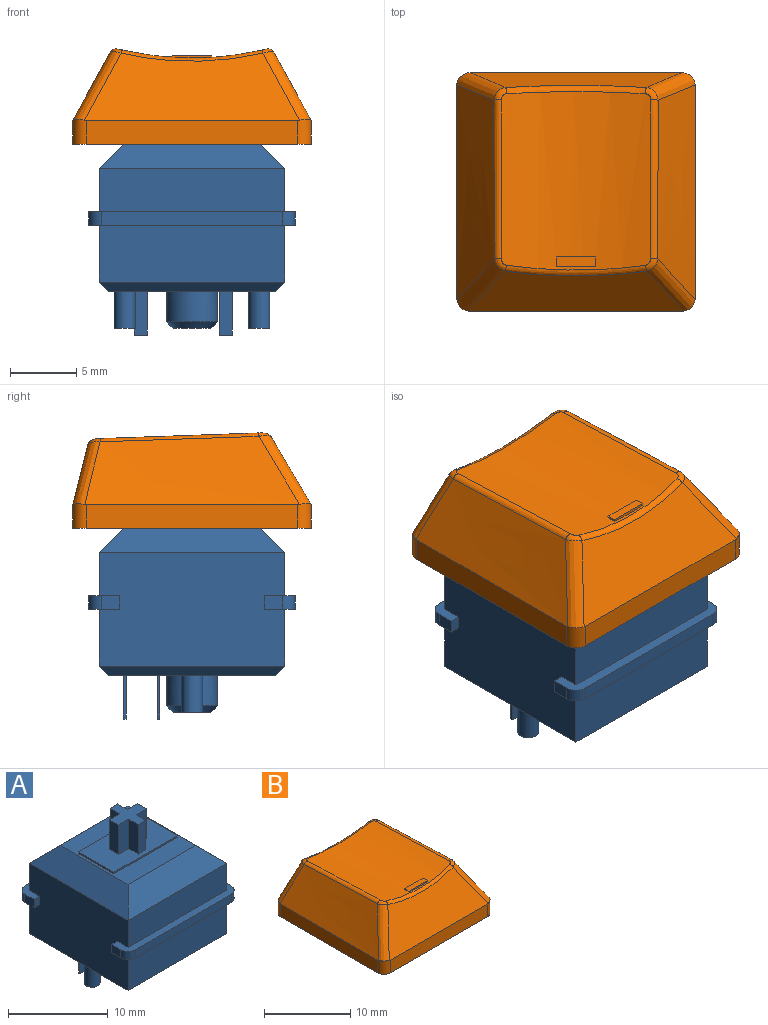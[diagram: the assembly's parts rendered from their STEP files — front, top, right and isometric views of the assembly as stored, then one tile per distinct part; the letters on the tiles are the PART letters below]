
ASSEMBLY  parts=2 mates=1
PART A: 69 faces, bbox 15.6x15.6x18.6 mm
  f0: plane 15.6x2.3mm, normal (0,0,-1), area 14.4mm2, adj f2,f3,f28,f30,f35,f60,f62,f63
  f1: plane 15.6x2.3mm, normal (0,0,-1), area 14.4mm2, adj f28,f30,f33,f34,f36,f59,f61,f64
  f2: plane 1.3x1mm, normal (1,0,0), area 1.3mm2, adj f0,f32,f62,f66
  f3: plane 1.3x1mm, normal (-1,0,0), area 1.3mm2, adj f0,f32,f63,f68
  f4: plane 15.6x2.3mm, normal (0,0,1), area 14.4mm2, adj f28,f30,f31,f33,f34,f36,f61,f64
  f5: plane 14x2.2mm, normal (-0.71,0,0.71), area 36.7mm2, adj f6,f7,f26,f30
  f6: plane 14x2.2mm, normal (0,-0.71,0.71), area 36.7mm2, adj f5,f7,f27,f31
  f7: plane 9.6x9.6mm, normal (0,0,1), area 47.2mm2, adj f5,f6,f8,f9,f10,f11,f26,f27
  f8: plane 5x0.2mm, normal (1,0,0), area 1mm2, adj f7,f9,f11,f12
  f9: plane 9x0.2mm, normal (0,1,0), area 1.8mm2, adj f7,f8,f10,f12
  f10: plane 5x0.2mm, normal (-1,0,0), area 1mm2, adj f7,f9,f11,f12
  f11: plane 9x0.2mm, normal (0,-1,0), area 1.8mm2, adj f7,f8,f10,f12
  f12: plane 9x5mm, normal (0,0,1), area 36.9mm2, adj f8,f9,f10,f11,f13,f14,f15,f16
  f13: plane 3.6x1.35mm, normal (1,0,0), area 4.9mm2, adj f12,f14,f24,f25
  f14: plane 3.6x1.08mm, normal (0,1,0), area 3.9mm2, adj f12,f13,f15,f25
  f15: plane 3.6x1.35mm, normal (-1,0,0), area 4.9mm2, adj f12,f14,f16,f25
  f16: plane 3.6x1.46mm, normal (0,1,0), area 5.3mm2, adj f12,f15,f17,f25
  f17: plane 3.6x1.3mm, normal (-1,0,0), area 4.7mm2, adj f12,f16,f18,f25
  f18: plane 3.6x1.46mm, normal (0,-1,0), area 5.3mm2, adj f12,f17,f19,f25
  f19: plane 3.6x1.35mm, normal (-1,0,0), area 4.9mm2, adj f12,f18,f20,f25
  f20: plane 3.6x1.08mm, normal (0,-1,0), area 3.9mm2, adj f12,f19,f21,f25
  f21: plane 3.6x1.35mm, normal (1,0,0), area 4.9mm2, adj f12,f20,f22,f25
  f22: plane 3.6x1.46mm, normal (0,-1,0), area 5.3mm2, adj f12,f21,f23,f25
  f23: plane 3.6x1.3mm, normal (1,0,0), area 4.7mm2, adj f12,f22,f24,f25
  f24: plane 3.6x1.46mm, normal (0,1,0), area 5.3mm2, adj f12,f13,f23,f25
  f25: plane 4x4mm, normal (0,0,1), area 8.1mm2, adj f13,f14,f15,f16,f17,f18,f19,f20
  f26: plane 14x2.2mm, normal (0,0.71,0.71), area 36.7mm2, adj f5,f7,f27,f29
  f27: plane 14x2.2mm, normal (0.71,0,0.71), area 36.7mm2, adj f6,f7,f26,f28
  f28: plane 14x8.6mm, normal (1,0,0), area 117.4mm2, adj f0,f1,f4,f27,f29,f31,f32,f55
  f29: plane 14x3.3mm, normal (0,1,0), area 46.2mm2, adj f26,f28,f30,f32
  f30: plane 14x8.6mm, normal (-1,0,0), area 117.4mm2, adj f0,f1,f4,f5,f29,f31,f32,f57
  f31: plane 14x3.3mm, normal (0,-1,0), area 46.2mm2, adj f4,f6,f28,f30
  f32: plane 15.6x2.3mm, normal (0,0,1), area 14.4mm2, adj f2,f3,f28,f29,f30,f35,f62,f63
  f33: plane 13.6x1mm, normal (0,-1,0), area 13.6mm2, adj f1,f4,f61,f64
  f34: plane 1.3x1mm, normal (1,0,0), area 1.3mm2, adj f1,f4,f61,f65
  f35: plane 13.6x1mm, normal (0,1,0), area 13.6mm2, adj f0,f32,f62,f63
  f36: plane 1.3x1mm, normal (-1,0,0), area 1.3mm2, adj f1,f4,f64,f67
  f37: plane 2.85x2.85mm, normal (0,0,-1), area 6.4mm2, adj f38
  f38: cone r=1.43mm half-angle=45deg, axis (0,0,1), area 7.4mm2, adj f37,f43
  f39: plane 1x0.2mm, normal (0,0,-1), area 0.2mm2, adj f44,f45,f46,f47
  f40: plane 1x0.2mm, normal (0,0,-1), area 0.2mm2, adj f48,f49,f50,f51
  f41: plane 1.6x1.6mm, normal (0,0,-1), area 2mm2, adj f52
  f42: plane 1.6x1.6mm, normal (0,0,-1), area 2mm2, adj f53
  f43: cylinder r=1.93mm len=3.85mm, axis (0,0,1), area 27.8mm2, adj f38,f54
  f44: plane 3.3x0.2mm, normal (-1,0,0), area 0.7mm2, adj f39,f45,f47,f54
  f45: plane 3.3x1mm, normal (0,1,0), area 3.3mm2, adj f39,f44,f46,f54
  f46: plane 3.3x0.2mm, normal (1,0,0), area 0.7mm2, adj f39,f45,f47,f54
  f47: plane 3.3x1mm, normal (0,-1,0), area 3.3mm2, adj f39,f44,f46,f54
  f48: plane 3.3x0.2mm, normal (-1,0,0), area 0.7mm2, adj f40,f49,f51,f54
  f49: plane 3.3x1mm, normal (0,1,0), area 3.3mm2, adj f40,f48,f50,f54
  f50: plane 3.3x0.2mm, normal (1,0,0), area 0.7mm2, adj f40,f49,f51,f54
  f51: plane 3.3x1mm, normal (0,-1,0), area 3.3mm2, adj f40,f48,f50,f54
  f52: cylinder r=0.8mm len=2.8mm, axis (0,0,1), area 14.1mm2, adj f41,f54
  f53: cylinder r=0.8mm len=2.8mm, axis (0,0,1), area 14.1mm2, adj f42,f54
  f54: plane 12.6x12.6mm, normal (0,0,-1), area 142.7mm2, adj f43,f44,f45,f46,f47,f48,f49,f50
  f55: plane 14x0.7mm, normal (0.71,0,-0.71), area 13.2mm2, adj f28,f54,f56,f58
  f56: plane 14x0.7mm, normal (0,0.71,-0.71), area 13.2mm2, adj f54,f55,f57,f60
  f57: plane 14x0.7mm, normal (-0.71,0,-0.71), area 13.2mm2, adj f30,f54,f56,f58
  f58: plane 14x0.7mm, normal (0,-0.71,-0.71), area 13.2mm2, adj f54,f55,f57,f59
  f59: plane 14x4.3mm, normal (0,-1,0), area 60.2mm2, adj f1,f28,f30,f58
  f60: plane 14x4.3mm, normal (0,1,0), area 60.2mm2, adj f0,f28,f30,f56
  f61: cylinder r=1mm len=1mm, axis (0,0,-1), area 1.6mm2, adj f1,f4,f33,f34
  f62: cylinder r=1mm len=1mm, axis (0,0,1), area 1.6mm2, adj f0,f2,f32,f35
  f63: cylinder r=1mm len=1mm, axis (0,0,-1), area 1.6mm2, adj f0,f3,f32,f35
  f64: cylinder r=1mm len=1mm, axis (0,0,1), area 1.6mm2, adj f1,f4,f33,f36
  f65: plane 1x0.8mm, normal (0,1,0), area 0.8mm2, adj f1,f4,f28,f34
  f66: plane 1x0.8mm, normal (0,-1,0), area 0.8mm2, adj f0,f2,f28,f32
  f67: plane 1x0.8mm, normal (0,1,0), area 0.8mm2, adj f1,f4,f30,f36
  f68: plane 1x0.8mm, normal (0,-1,0), area 0.8mm2, adj f0,f3,f30,f32
PART B: 55 faces, bbox 21.6x21x10.3 mm
  f0: cylinder r=22.9mm len=13.32mm, axis (0,1,-0.04), area 147.4mm2, adj f18,f19,f20,f21,f22,f23,f24,f25
  f1: plane 18x18mm, normal (0,0,-1), area 67.1mm2, adj f2,f3,f4,f5,f10,f12,f14,f16
  f2: plane 16x1.8mm, normal (1,0,0), area 28.8mm2, adj f1,f9,f10,f16
  f3: plane 16x1.8mm, normal (0,1,0), area 28.8mm2, adj f1,f6,f14,f15,f16,f17
  f4: plane 16x1.8mm, normal (-1,0,0), area 28.8mm2, adj f1,f7,f12,f14
  f5: plane 16x1.8mm, normal (0,-1,0), area 28.8mm2, adj f1,f8,f10,f12
  f6: plane 15.96x4.48mm, normal (0,0.97,0.24), area 56.8mm2, adj f3,f15,f17,f20
  f7: bspline ~18x5.51mm, area 80.2mm2, adj f4,f12,f13,f14,f15,f19
  f8: plane 16.27x5.09mm, normal (0,-0.86,0.51), area 74.6mm2, adj f5,f10,f11,f12,f13,f23
  f9: bspline ~18x5.51mm, area 80.2mm2, adj f2,f10,f11,f16,f17,f24
  f10: cylinder r=1mm len=1.89mm, axis (0,0,-1), area 2.9mm2, adj f1,f2,f5,f8,f9,f11
  f11: bspline ~6.77x4.7mm, area 8.7mm2, adj f8,f9,f10,f25
  f12: cylinder r=1mm len=1.89mm, axis (0,0,1), area 2.9mm2, adj f1,f4,f5,f7,f8,f13
  f13: bspline ~6.77x4.7mm, area 8.7mm2, adj f7,f8,f12,f21
  f14: cylinder r=1mm len=1.81mm, axis (0,0,-1), area 2.8mm2, adj f1,f3,f4,f7,f15
  f15: bspline ~8.13x5.44mm, area 7.9mm2, adj f3,f6,f7,f14,f18
  f16: cylinder r=1mm len=1.81mm, axis (0,0,1), area 2.8mm2, adj f1,f2,f3,f9,f17
  f17: bspline ~8.13x5.44mm, area 7.9mm2, adj f3,f6,f9,f16,f22
  f18: bspline ~1.19x1.01mm, area 0.7mm2, adj f0,f15,f19,f20
  f19: bspline ~16.72x0.91mm, area 7.8mm2, adj f0,f7,f18,f21
  f20: bspline ~10.66x0.99mm, area 6.9mm2, adj f0,f6,f18,f22
  f21: bspline ~1.2x1.09mm, area 0.6mm2, adj f0,f13,f19,f23
  f22: bspline ~1.17x1.02mm, area 0.7mm2, adj f0,f17,f20,f24
  f23: bspline ~10.72x0.84mm, area 5.8mm2, adj f0,f8,f21,f25
  f24: bspline ~16.72x0.91mm, area 7.8mm2, adj f0,f9,f22,f25
  f25: bspline ~1.2x1.09mm, area 0.6mm2, adj f0,f11,f23,f24
  f26: plane 16.02x1.56mm, normal (-1,0,0), area 24.6mm2, adj f1,f27,f29,f33
  f27: plane 16x1.68mm, normal (0,-1,0), area 26.8mm2, adj f1,f26,f28,f30,f31,f33
  f28: plane 16.02x1.56mm, normal (1,0,0), area 24.6mm2, adj f1,f27,f29,f31
  f29: plane 16.02x1.54mm, normal (0,1,0), area 24.4mm2, adj f1,f26,f28,f32
  f30: plane 16.19x4.4mm, normal (0,-0.97,-0.24), area 50.7mm2, adj f27,f31,f33,f34
  f31: offset ~20x7.51mm, area 71.4mm2, adj f27,f28,f30,f32,f34
  f32: plane 16.71x5.3mm, normal (0,0.86,-0.51), area 66.9mm2, adj f29,f31,f33,f34
  f33: offset ~20x7.51mm, area 71.4mm2, adj f26,f27,f30,f32,f34
  f34: cylinder r=23.9mm len=12.29mm, axis (0,1,-0.04), area 112.6mm2, adj f30,f31,f32,f33,f46
  f35: plane 4.69x1.5mm, normal (-1,0,0), area 7mm2, adj f36,f44,f45,f49
  f36: plane 4.78x1.5mm, normal (0,-1,0), area 7.1mm2, adj f35,f37,f45,f49
  f37: plane 4.82x1.3mm, normal (-1,0,0), area 6.2mm2, adj f36,f38,f45,f49
  f38: plane 4.82x1.5mm, normal (0,1,0), area 7.2mm2, adj f37,f39,f45,f49
  f39: plane 4.79x1.5mm, normal (-1,0,0), area 7.1mm2, adj f38,f40,f45,f49
  f40: plane 4.79x1.3mm, normal (0,1,0), area 6.2mm2, adj f39,f41,f45,f49
  f41: plane 4.79x1.5mm, normal (1,0,0), area 7.1mm2, adj f40,f42,f45,f49
  f42: plane 4.82x1.5mm, normal (0,1,0), area 7.2mm2, adj f41,f43,f45,f49
  f43: plane 4.82x1.3mm, normal (1,0,0), area 6.2mm2, adj f42,f45,f47,f49
  f44: plane 4.64x1.3mm, normal (0,-1,0), area 6mm2, adj f35,f45,f48,f49
  f45: plane 5.5x5.5mm, normal (0,0,-1), area 14.3mm2, adj f35,f36,f37,f38,f39,f40,f41,f42
  f46: cylinder r=2.75mm len=5.5mm, axis (0,0,-1), area 84mm2, adj f34,f45
  f47: plane 4.78x1.5mm, normal (0,-1,0), area 7.1mm2, adj f43,f45,f48,f49
  f48: plane 4.69x1.5mm, normal (1,0,0), area 7mm2, adj f44,f45,f47,f49
  f49: cylinder r=23.9mm len=4.3mm, axis (0,1,-0.04), area 9.5mm2, adj f35,f36,f37,f38,f39,f40,f41,f42
  f50: plane 0.71x0.18mm, normal (1,0,0), area 0.1mm2, adj f0,f51,f53,f54
  f51: plane 3x0.2mm, normal (0,1,-0.04), area 0.6mm2, adj f0,f50,f52,f54
  f52: plane 0.71x0.18mm, normal (-1,0,0), area 0.1mm2, adj f0,f51,f53,f54
  f53: plane 3x0.2mm, normal (0,-1,0.04), area 0.6mm2, adj f0,f50,f52,f54
  f54: plane 3x0.7mm, normal (0,0.04,1), area 2.1mm2, adj f50,f51,f52,f53
PLACE A at identity fixed
PLACE B t=(0,0,11.1)mm
MATE fastened B.f46 <-> A.f38  axis (0,0,-1) through (0,0,11.7)mm
